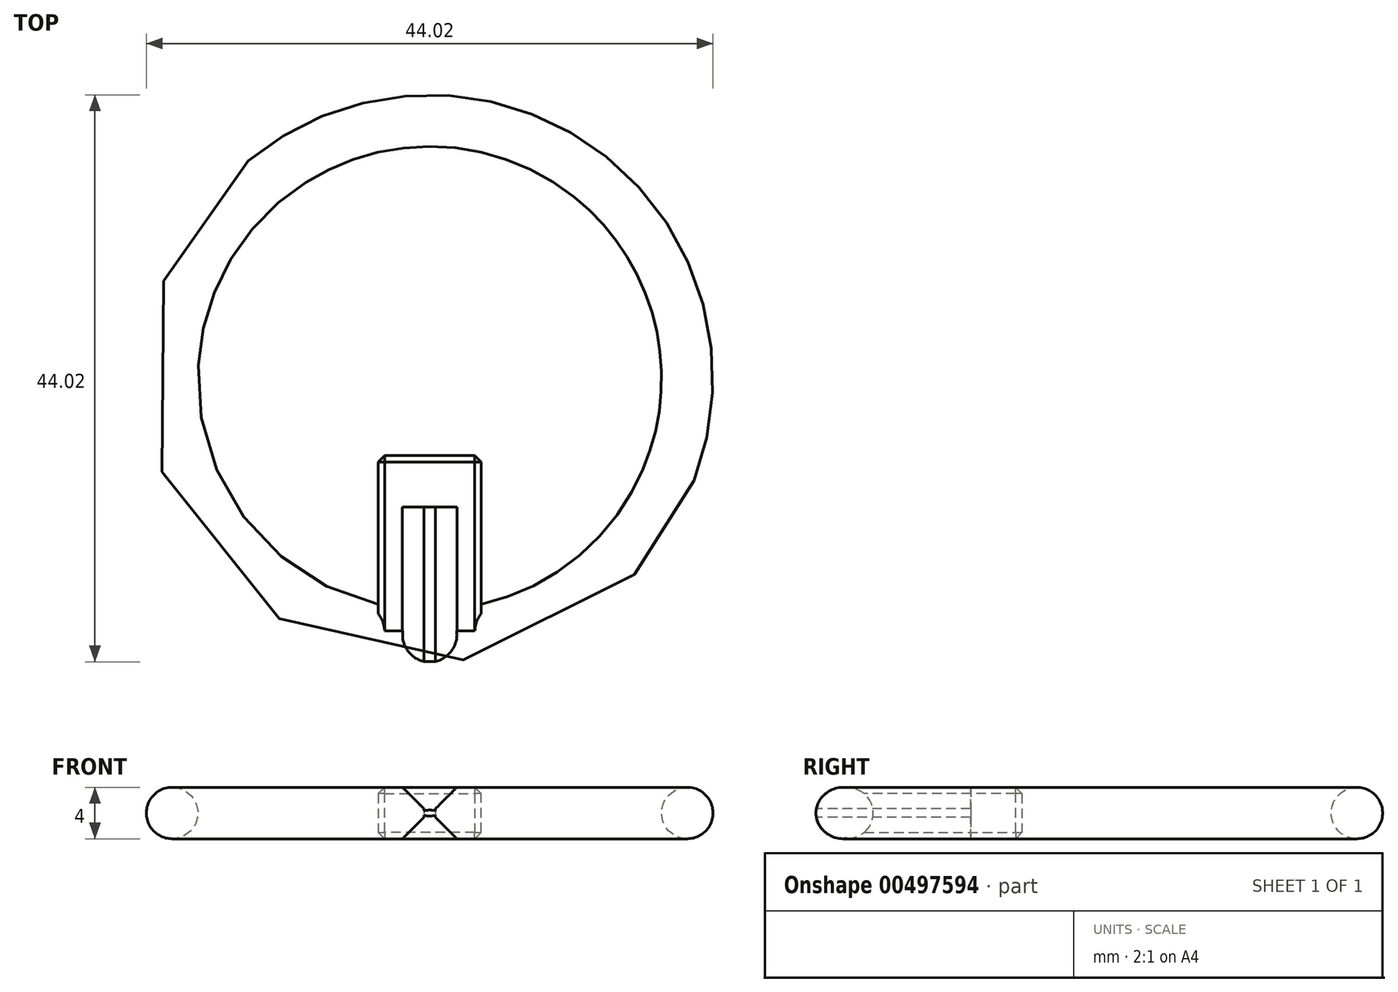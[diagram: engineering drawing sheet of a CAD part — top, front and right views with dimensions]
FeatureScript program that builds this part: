
annotation { "Feature Type Name" : "Feature", "Feature Type Description" : "" }
export const myFeature = defineFeature(function(context is Context, id is Id, definition is map)
    precondition{}
    {
        {
            var Q0;
            Q0=qCreatedBy(makeId("Top.planeOp"),FACE);
            var sketch = newSketch(context, id + "F0", { "sketchPlane" : qUnion([Q0])});
            skLineSegment(sketch, "E0", {"start": v(4, -8) * mm, "end": v(-4, -8) * mm});
            skLineSegment(sketch, "E1", {"start": v(-4, -8) * mm, "end": v(-4, -19.6) * mm});
            skLineSegment(sketch, "E2", {"start": v(-4, -19.6) * mm, "end": v(4, -19.6) * mm});
            skLineSegment(sketch, "E3", {"start": v(4, -19.6) * mm, "end": v(4, -8) * mm});
            skCircle(sketch, "E4", {"center": v(0, 0) * mm, "radius": 20 * mm});
            skLineSegment(sketch, "E5", {"start": v(-4, -8) * mm, "end": v(-4, -6) * mm});
            skLineSegment(sketch, "E6", {"start": v(-4, -6) * mm, "end": v(4, -6) * mm});
            skLineSegment(sketch, "E7", {"start": v(4, -6) * mm, "end": v(4, -8) * mm});
            skSolve(sketch);
        }
        {
            var Q0;
            Q0=qCreatedBy(makeId("Front.planeOp"),FACE);
            var sketch = newSketch(context, id + "F1", { "sketchPlane" : qUnion([Q0])});
            skCircle(sketch, "E8", {"center": v(20.01, 0) * mm, "radius": 2 * mm});
            skSolve(sketch);
        }
        {
            var Q0;
            Q0=makeQuery(id+"F1.imprint","IMPRINT",FACE,{"disambiguationData":[TD([[makeQuery(id+"F1.imprint","IMPRINT",EDGE,{"derivedFrom":sQuery(id+"F1.wireOp",EDGE,"E8")}),1.0]])]});
            var Q1;
            Q1=sQuery(id+"F0.wireOp",EDGE,"E4");
            revolve(context, id + "F2", {"entities" : qUnion([Q0]), "axis" : qUnion([Q1]), "revolveType" : RevolveType.FULL});
        }
        {
            var Q0;
            Q0=makeQuery(id+"F0.imprint","IMPRINT",FACE,{"disambiguationData":[TD([[makeQuery(id+"F0.imprint","IMPRINT",EDGE,{"derivedFrom":sQuery(id+"F0.wireOp",EDGE,"E0")}),1.0]])]});
            var Q1;
            Q1=makeQuery(id+"F0.imprint","IMPRINT",FACE,{"disambiguationData":[TD([[makeQuery(id+"F0.imprint","IMPRINT",EDGE,{"derivedFrom":sQuery(id+"F0.wireOp",EDGE,"E0")}),-1.0]])]});
            extrude(context, id + "F3", {"entities" : qUnion([Q0, Q1]), "operationType" : NewBodyOperationType.ADD, "depth" : 2 * mm, "hasSecondDirection" : true, "secondDirectionOppositeDirection" : true, "secondDirectionDepth" : 2 * mm});
        }
        {
            var Q0;
            Q0=makeQuery(id+"F3.opExtrude","SWEPT_FACE",FACE,{"disambiguationData":[OSD([sQuery(id+"F0.wireOp",EDGE,"E6")])]});
            cPlane(context, id + "F4", {"entities" : qUnion([Q0]), "cplaneType" : CPlaneType.OFFSET, "offset" : 16 * mm, "oppositeDirection" : true, "width" : 150 * mm, "height" : 150 * mm});
        }
        {
            var Q0;
            Q0=qCreatedBy(id+"F4.planeOp",FACE);
            var sketch = newSketch(context, id + "F5", { "sketchPlane" : qUnion([Q0])});
            skLineSegment(sketch, "E9", {"start": v(-2, 2) * mm, "end": v(-0.36, 0.36) * mm});
            skLineSegment(sketch, "E10", {"start": v(0.36, 0.36) * mm, "end": v(2, 2) * mm});
            skLineSegment(sketch, "E11", {"start": v(-0.37, -0.37) * mm, "end": v(-2, -2) * mm});
            skLineSegment(sketch, "E12", {"start": v(-2, -2) * mm, "end": v(2, -2) * mm});
            skLineSegment(sketch, "E13", {"start": v(2, -2) * mm, "end": v(0.36, -0.36) * mm});
            skLineSegment(sketch, "E14", {"start": v(2, 2) * mm, "end": v(-2, 2) * mm});
            skLineSegment(sketch, "E15.bottom", {"start": v(-0.36, 0.36) * mm, "end": v(-0.37, 0.36) * mm});
            skLineSegment(sketch, "E15.left", {"start": v(0.36, 0.36) * mm, "end": v(0.36, -0.37) * mm});
            skLineSegment(sketch, "E15.right", {"start": v(-0.37, 0.36) * mm, "end": v(-0.37, -0.37) * mm});
            skLineSegment(sketch, "E16.0", {"start": v(0.44, 0.33) * mm, "end": v(0.44, -0.33) * mm});
            skLineSegment(sketch, "E16.1", {"start": v(2.2, -2.08) * mm, "end": v(0.44, -0.33) * mm});
            skLineSegment(sketch, "E16.2", {"start": v(0.44, 0.33) * mm, "end": v(2.2, 2.08) * mm});
            skLineSegment(sketch, "E16.3", {"start": v(-2.2, -2.08) * mm, "end": v(2.2, -2.08) * mm});
            skLineSegment(sketch, "E16.4", {"start": v(2.2, 2.08) * mm, "end": v(-2.2, 2.08) * mm});
            skLineSegment(sketch, "E16.5", {"start": v(-2.2, 2.08) * mm, "end": v(-0.45, 0.34) * mm});
            skLineSegment(sketch, "E16.6", {"start": v(-0.45, 0.34) * mm, "end": v(-0.45, -0.34) * mm});
            skLineSegment(sketch, "E16.7", {"start": v(-0.45, -0.34) * mm, "end": v(-2.2, -2.08) * mm});
            skSolve(sketch);
        }
        {
            var Q0;
            Q0=makeQuery(id+"F5.imprint","IMPRINT",FACE,{"disambiguationData":[TD([[makeQuery(id+"F5.imprint","IMPRINT",EDGE,{"derivedFrom":sQuery(id+"F5.wireOp",EDGE,"E9")}),-1.0]])]});
            var Q1;
            Q1=makeQuery(id+"F5.imprint","IMPRINT",FACE,{"disambiguationData":[TD([[makeQuery(id+"F5.imprint","IMPRINT",EDGE,{"derivedFrom":sQuery(id+"F5.wireOp",EDGE,"E9")}),1.0]])]});
            extrude(context, id + "F6", {"entities" : qUnion([Q0, Q1]), "operationType" : NewBodyOperationType.REMOVE, "depth" : 12 * mm});
        }
        {
            var Q0;
            Q0=makeQuery(id+"F3.opExtrude","CAP_EDGE",EDGE,{"disambiguationData":[OSD([sQuery(id+"F0.wireOp",EDGE,"E1")])],"isStart":false});
            var Q1;
            Q1=makeQuery(id+"F3.opExtrude","CAP_EDGE",EDGE,{"disambiguationData":[OSD([sQuery(id+"F0.wireOp",EDGE,"E0")])],"isStart":false});
            var Q2;
            Q2=makeQuery(id+"F3.opExtrude","CAP_EDGE",EDGE,{"disambiguationData":[OSD([sQuery(id+"F0.wireOp",EDGE,"E3")])],"isStart":false});
            var Q3;
            Q3=makeQuery(id+"F3.opExtrude","CAP_EDGE",EDGE,{"disambiguationData":[OSD([sQuery(id+"F0.wireOp",EDGE,"E3")])],"isStart":true});
            var Q4;
            Q4=makeQuery(id+"F3.opExtrude","CAP_EDGE",EDGE,{"disambiguationData":[OSD([sQuery(id+"F0.wireOp",EDGE,"E1")])],"isStart":true});
            var Q5;
            Q5=makeQuery(id+"F3.opExtrude","CAP_EDGE",EDGE,{"disambiguationData":[OSD([sQuery(id+"F0.wireOp",EDGE,"E0")])],"isStart":true});
            var Q6;
            Q6=makeQuery(id+"F3.opExtrude","CAP_EDGE",EDGE,{"disambiguationData":[OSD([sQuery(id+"F0.wireOp",EDGE,"E6")])],"isStart":true});
            var Q7;
            Q7=makeQuery(id+"F3.opExtrude","CAP_EDGE",EDGE,{"disambiguationData":[OSD([sQuery(id+"F0.wireOp",EDGE,"E6")])],"isStart":false});
            var Q8;
            Q8=makeQuery(id+"F3.opExtrude","SWEPT_EDGE",EDGE,{"disambiguationData":[OSD([sQuery(id+"F0.wireOp",EDGE,"E6"),sQuery(id+"F0.wireOp",EDGE,"E7")])]});
            var Q9;
            Q9=makeQuery(id+"F3.opExtrude","SWEPT_EDGE",EDGE,{"disambiguationData":[OSD([sQuery(id+"F0.wireOp",EDGE,"E5"),sQuery(id+"F0.wireOp",EDGE,"E6")])]});
            chamfer(context, id + "F7", {"entities" : qUnion([Q0, Q1, Q2, Q3, Q4, Q5, Q6, Q7, Q8, Q9]), "width" : .5 * mm, "tangentPropagation" : true});
        }
    });
